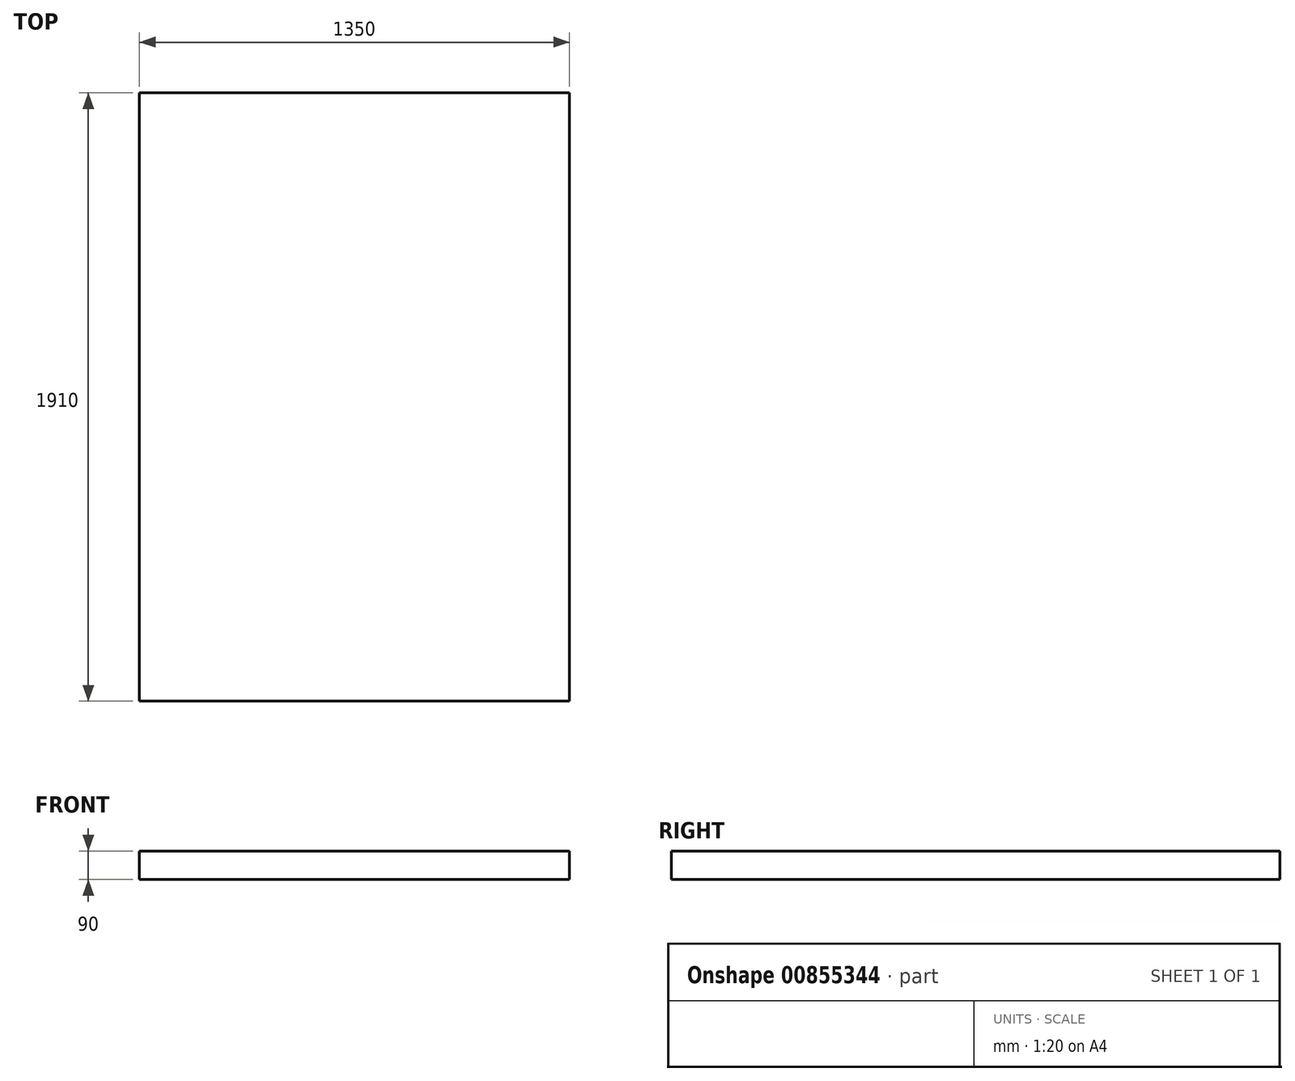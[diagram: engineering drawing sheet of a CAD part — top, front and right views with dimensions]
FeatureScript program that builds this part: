
annotation { "Feature Type Name" : "Feature", "Feature Type Description" : "" }
export const myFeature = defineFeature(function(context is Context, id is Id, definition is map)
    precondition{}
    {
        {
            var Q0;
            Q0=qCreatedBy(makeId("Top.planeOp"),FACE);
            var sketch = newSketch(context, id + "F0", { "sketchPlane" : qUnion([Q0])});
            skLineSegment(sketch, "E0.bottom", {"start": v(0, 0) * mm, "end": v(1350, 0) * mm});
            skLineSegment(sketch, "E0.top", {"start": v(0, 1910) * mm, "end": v(1350, 1910) * mm});
            skLineSegment(sketch, "E0.left", {"start": v(0, 0) * mm, "end": v(0, 1910) * mm});
            skLineSegment(sketch, "E0.right", {"start": v(1350, 0) * mm, "end": v(1350, 1910) * mm});
            skSolve(sketch);
        }
        {
            var Q0;
            Q0 = qSketchRegion(id + "F0", true);
            extrude(context, id + "F1", {"entities" : qUnion([Q0]), "depth" : 90 * mm, "offsetDistance" : 25 * mm});
        }
    });
